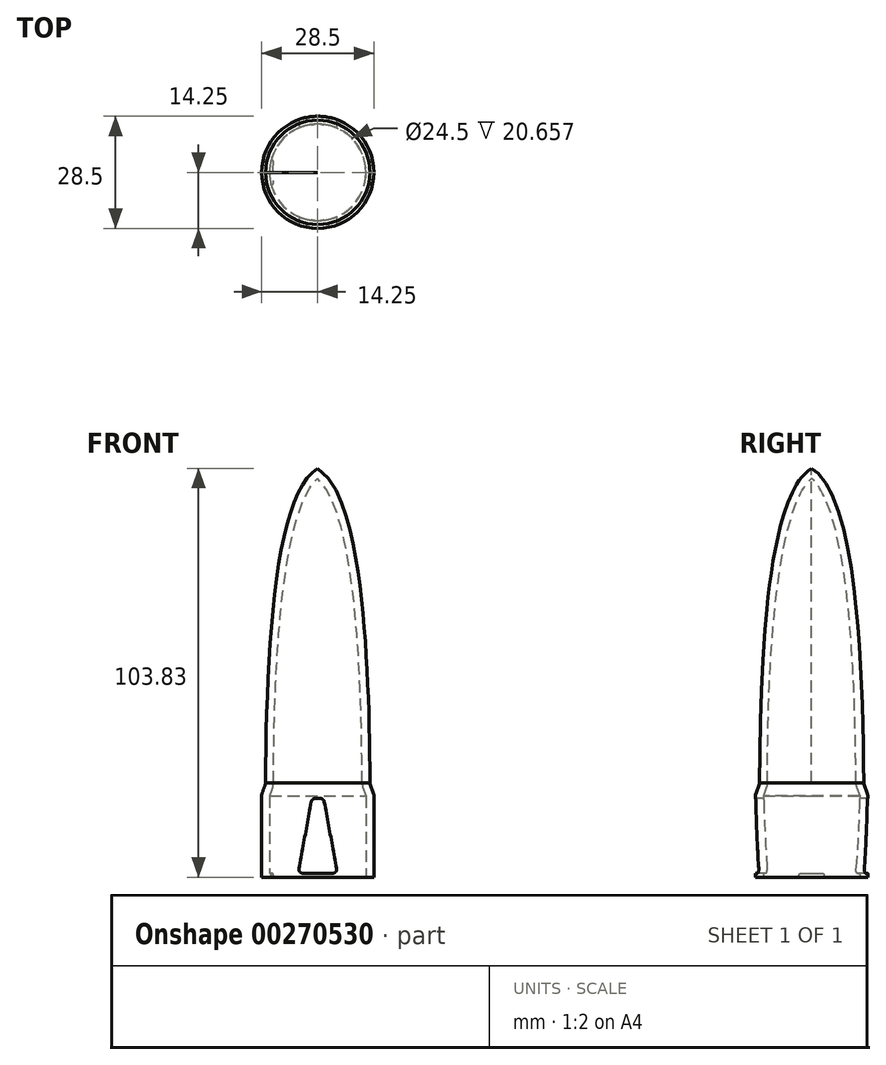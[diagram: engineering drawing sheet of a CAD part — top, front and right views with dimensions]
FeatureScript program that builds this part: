
annotation { "Feature Type Name" : "Feature", "Feature Type Description" : "" }
export const myFeature = defineFeature(function(context is Context, id is Id, definition is map)
    precondition{}
    {
        {
            var Q0;
            Q0=qCreatedBy(makeId("Front.planeOp"),FACE);
            var sketch = newSketch(context, id + "F0", { "sketchPlane" : qUnion([Q0])});
            skLineSegment(sketch, "E0", {"start": v(-14.25, 0) * mm, "end": v(-14.25, 20.83) * mm});
            skLineSegment(sketch, "E1", {"start": v(-14.2, 21.16) * mm, "end": v(-13.3, 23.67) * mm});
            skFitSpline(sketch, "E2", {"points": [v(-13.25, 23.83) * mm, v(0, 103.83) * mm], "startDerivative": vector(0.41, 98.91) * mm, "endDerivative": vector(33.26, 19.54) * mm});
            skArc(sketch, "E3.filletArc", {"start": v(-13.3, 23.67) * mm, "mid": v(-13.26, 23.83) * mm, "end": v(-13.25, 24) * mm});
            skPoint(sketch, "E4.visualSharp", {"position": v(-14.25, 21) * mm});
            skArc(sketch, "E4.filletArc", {"start": v(-14.2, 21.16) * mm, "mid": v(-14.24, 21) * mm, "end": v(-14.25, 20.83) * mm});
            skLineSegment(sketch, "E5", {"start": v(-14.25, 0) * mm, "end": v(0, 0) * mm});
            skLineSegment(sketch, "E6", {"start": v(0, 0) * mm, "end": v(0, 103.83) * mm});
            skSolve(sketch);
        }
        {
            var Q0;
            Q0=makeQuery(id+"F0.imprint","IMPRINT",FACE,{"disambiguationData":[TD([[makeQuery(id+"F0.imprint","IMPRINT",EDGE,{"derivedFrom":sQuery(id+"F0.wireOp",EDGE,"E0")}),-1.0]])]});
            var Q1;
            Q1=sQuery(id+"F0.wireOp",EDGE,"E6");
            revolve(context, id + "F1", {"entities" : qUnion([Q0]), "axis" : qUnion([Q1]), "revolveType" : RevolveType.FULL});
        }
        {
            var Q0;
            Q0=makeQuery(id+"F1.opRevolve","SWEPT_FACE",FACE,{"disambiguationData":[OSD([sQuery(id+"F0.wireOp",EDGE,"E5")])]});
            shell(context, id + "F2", {"entities" : qUnion([Q0]), "thickness" : 2 * mm});
        }
        {
            var Q0;
            Q0=qCreatedBy(makeId("Front.planeOp"),FACE);
            var sketch = newSketch(context, id + "F3", { "sketchPlane" : qUnion([Q0])});
            skLineSegment(sketch, "E7.bottom", {"start": v(-12.25, 0) * mm, "end": v(-12.05, 0) * mm});
            skLineSegment(sketch, "E7.top", {"start": v(-12.25, 1) * mm, "end": v(-12.05, 1) * mm});
            skLineSegment(sketch, "E7.left", {"start": v(-12.25, 0) * mm, "end": v(-12.25, 1) * mm});
            skLineSegment(sketch, "E7.right", {"start": v(-11.55, 0.5) * mm, "end": v(-11.55, 0.5) * mm});
            skPoint(sketch, "E8.visualSharp", {"position": v(-11.55, 1) * mm});
            skArc(sketch, "E8.filletArc", {"start": v(-11.55, 0.5) * mm, "mid": v(-11.7, 0.85) * mm, "end": v(-12.05, 1) * mm});
            skPoint(sketch, "E9.visualSharp", {"position": v(-11.55, 0) * mm});
            skArc(sketch, "E9.filletArc", {"start": v(-12.05, 0) * mm, "mid": v(-11.7, 0.15) * mm, "end": v(-11.55, 0.5) * mm});
            skSolve(sketch);
        }
        {
            var Q0;
            Q0=makeQuery(id+"F3.imprint","IMPRINT",FACE,{"disambiguationData":[TD([[makeQuery(id+"F3.imprint","IMPRINT",EDGE,{"derivedFrom":sQuery(id+"F3.wireOp",EDGE,"E7.bottom")}),1.0]])]});
            var Q1;
            Q1=sQuery(id+"F0.wireOp",EDGE,"E6");
            revolve(context, id + "F4", {"operationType" : NewBodyOperationType.ADD, "entities" : qUnion([Q0]), "axis" : qUnion([Q1]), "revolveType" : RevolveType.SYMMETRIC, "angle" : 30 * degree});
        }
        {
            var Q0;
            Q0=makeQuery(id+"F4.opRevolve","CAP_EDGE",EDGE,{"disambiguationData":[OSD([sQuery(id+"F3.wireOp",EDGE,"E8.filletArc"),sQuery(id+"F3.wireOp",EDGE,"E9.filletArc")])],"isStart":false});
            var Q1;
            Q1=makeQuery(id+"F4.opRevolve","CAP_EDGE",EDGE,{"disambiguationData":[OSD([sQuery(id+"F3.wireOp",EDGE,"E8.filletArc"),sQuery(id+"F3.wireOp",EDGE,"E9.filletArc")])],"isStart":true});
            var Q2;
            Q2=makeQuery(id+"FgE5xWMmyorXorw_1.1.F4.opRevolve","CAP_EDGE",EDGE,{"disambiguationData":[OSD([sQuery(id+"F3.wireOp",EDGE,"E8.filletArc"),sQuery(id+"F3.wireOp",EDGE,"E9.filletArc")])],"isStart":false});
            var Q3;
            Q3=makeQuery(id+"FgE5xWMmyorXorw_1.1.F4.opRevolve","CAP_EDGE",EDGE,{"disambiguationData":[OSD([sQuery(id+"F3.wireOp",EDGE,"E8.filletArc"),sQuery(id+"F3.wireOp",EDGE,"E9.filletArc")])],"isStart":true});
            fillet(context, id + "F5", {"entities" : qUnion([Q0, Q1, Q2, Q3]), "radius" : .5 * mm, "tangentPropagation" : true, "allowEdgeOverflow" : false});
        }
        {
            var Q0;
            Q0=qCreatedBy(makeId("Front.planeOp"),FACE);
            var sketch = newSketch(context, id + "F6", { "sketchPlane" : qUnion([Q0])});
            skLineSegment(sketch, "E10", {"start": v(-3.8, 1) * mm, "end": v(3.8, 1) * mm});
            skLineSegment(sketch, "E11", {"start": v(4.78, 2.18) * mm, "end": v(1.65, 19.18) * mm});
            skLineSegment(sketch, "E12", {"start": v(0.67, 20) * mm, "end": v(-0.67, 20) * mm});
            skLineSegment(sketch, "E13", {"start": v(-1.65, 19.18) * mm, "end": v(-4.78, 2.18) * mm});
            skPoint(sketch, "E14.visualSharp", {"position": v(1.5, 20) * mm});
            skArc(sketch, "E14.filletArc", {"start": v(1.65, 19.18) * mm, "mid": v(1.3, 19.77) * mm, "end": v(0.67, 20) * mm});
            skPoint(sketch, "E15.visualSharp", {"position": v(-1.5, 20) * mm});
            skArc(sketch, "E15.filletArc", {"start": v(-0.67, 20) * mm, "mid": v(-1.3, 19.77) * mm, "end": v(-1.65, 19.18) * mm});
            skPoint(sketch, "E16.visualSharp", {"position": v(-5, 1) * mm});
            skArc(sketch, "E16.filletArc", {"start": v(-4.78, 2.18) * mm, "mid": v(-4.57, 1.36) * mm, "end": v(-3.8, 1) * mm});
            skPoint(sketch, "E17.visualSharp", {"position": v(5, 1) * mm});
            skArc(sketch, "E17.filletArc", {"start": v(3.8, 1) * mm, "mid": v(4.57, 1.36) * mm, "end": v(4.78, 2.18) * mm});
            skSolve(sketch);
        }
        {
            var Q0;
            Q0 = qSketchRegion(id + "F6", true);
            extrude(context, id + "F7", {"entities" : qUnion([Q0]), "operationType" : NewBodyOperationType.REMOVE, "endBound" : BoundingType.SYMMETRIC, "oppositeDirection" : true, "depth" : 50 * mm});
        }
    });
